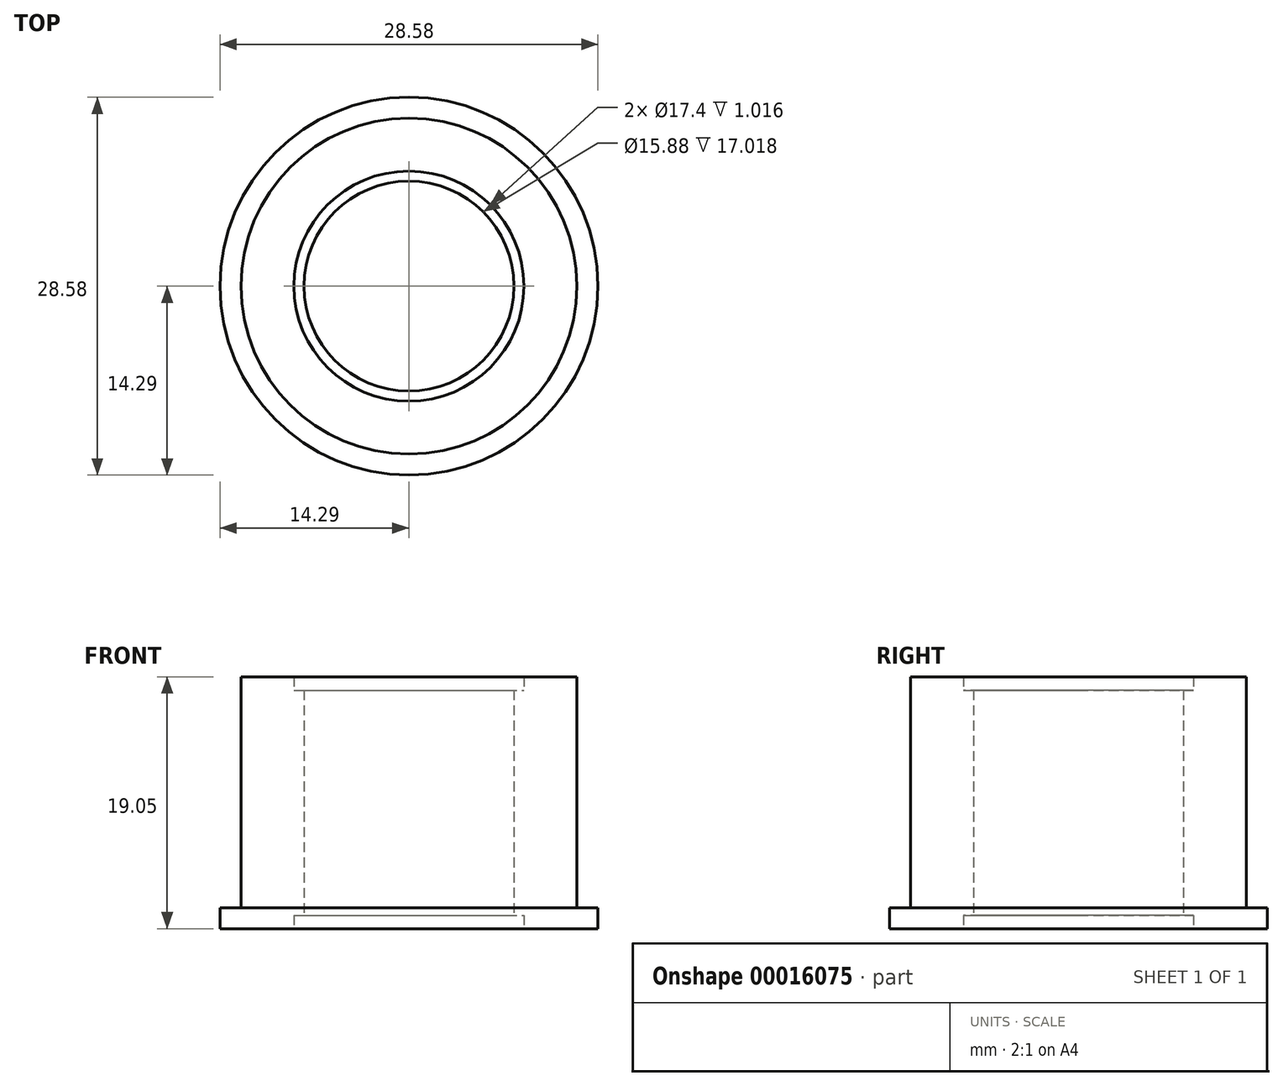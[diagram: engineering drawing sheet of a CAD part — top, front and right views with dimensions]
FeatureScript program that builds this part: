
annotation { "Feature Type Name" : "Feature", "Feature Type Description" : "" }
export const myFeature = defineFeature(function(context is Context, id is Id, definition is map)
    precondition{}
    {
        {
            var Q0;
            Q0=qCreatedBy(makeId("Front.planeOp"),FACE);
            var sketch = newSketch(context, id + "F0", { "sketchPlane" : qUnion([Q0])});
            skLineSegment(sketch, "E0", {"start": v(8.7, 0) * mm, "end": v(14.29, 0) * mm});
            skLineSegment(sketch, "E1", {"start": v(14.29, 0) * mm, "end": v(14.29, 1.59) * mm});
            skLineSegment(sketch, "E2", {"start": v(14.29, 1.59) * mm, "end": v(12.7, 1.59) * mm});
            skLineSegment(sketch, "E3", {"start": v(12.7, 1.59) * mm, "end": v(12.7, 19.05) * mm});
            skLineSegment(sketch, "E4", {"start": v(12.7, 19.05) * mm, "end": v(8.7, 19.05) * mm});
            skLineSegment(sketch, "E5", {"start": v(8.7, 19.05) * mm, "end": v(8.7, 18.03) * mm});
            skLineSegment(sketch, "E6", {"start": v(8.7, 18.03) * mm, "end": v(7.94, 18.03) * mm});
            skLineSegment(sketch, "E7", {"start": v(7.94, 18.03) * mm, "end": v(7.94, 1.02) * mm});
            skLineSegment(sketch, "E8", {"start": v(7.94, 1.02) * mm, "end": v(8.7, 1.02) * mm});
            skLineSegment(sketch, "E9", {"start": v(8.7, 1.02) * mm, "end": v(8.7, 0) * mm});
            skLineSegment(sketch, "E10", {"start": v(0, 0) * mm, "end": v(0, 19.05) * mm, "construction": true});
            skSolve(sketch);
        }
        {
            var Q0;
            Q0 = qSketchRegion(id + "F0", true);
            var Q1;
            Q1=sQuery(id+"F0.wireOp",EDGE,"E10");
            revolve(context, id + "F1", {"entities" : qUnion([Q0]), "axis" : qUnion([Q1]), "revolveType" : RevolveType.FULL});
        }
    });
